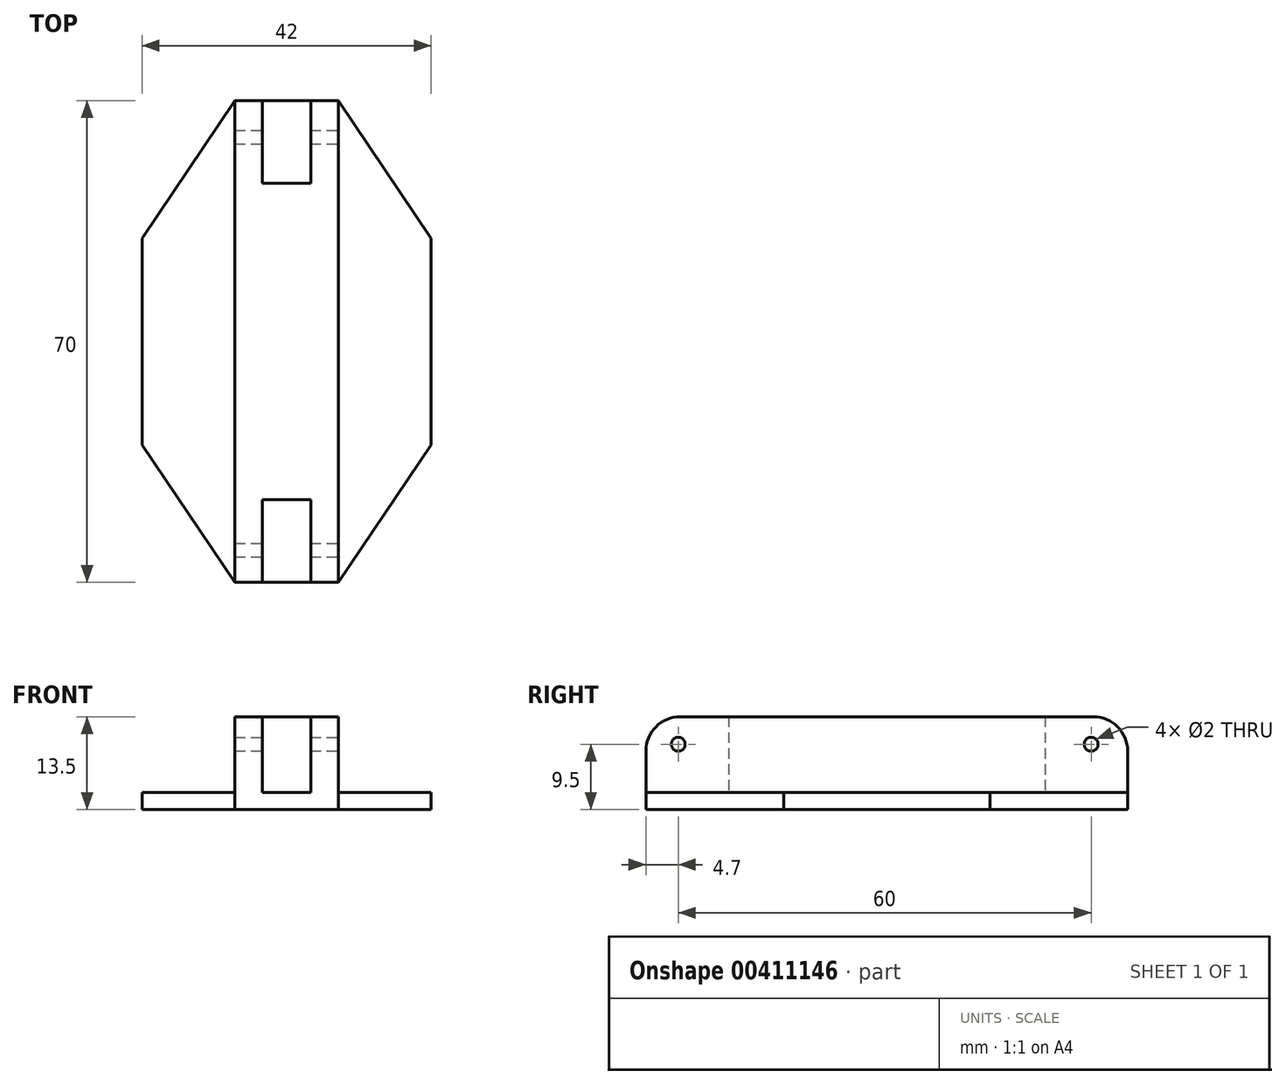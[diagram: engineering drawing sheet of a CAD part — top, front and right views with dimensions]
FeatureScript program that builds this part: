
annotation { "Feature Type Name" : "Feature", "Feature Type Description" : "" }
export const myFeature = defineFeature(function(context is Context, id is Id, definition is map)
    precondition{}
    {
        {
            var Q0;
            Q0=qCreatedBy(makeId("Top.planeOp"),FACE);
            var sketch = newSketch(context, id + "F0", { "sketchPlane" : qUnion([Q0])});
            skLineSegment(sketch, "E0.bottom", {"start": v(-7.14, 35.3) * mm, "end": v(7.86, 35.3) * mm});
            skLineSegment(sketch, "E0.top", {"start": v(-7.14, -34.7) * mm, "end": v(7.86, -34.7) * mm});
            skLineSegment(sketch, "E0.left", {"start": v(-20.64, 15.3) * mm, "end": v(-20.64, -14.7) * mm});
            skLineSegment(sketch, "E0.right", {"start": v(21.36, 15.3) * mm, "end": v(21.36, -14.7) * mm});
            skPoint(sketch, "E0.middle", {"position": v(0.36, 0.3) * mm});
            skLineSegment(sketch, "E1", {"start": v(-7.14, 35.3) * mm, "end": v(-7.14, 15.3) * mm});
            skLineSegment(sketch, "E2", {"start": v(-7.14, 15.3) * mm, "end": v(-20.64, 15.3) * mm});
            skLineSegment(sketch, "E3", {"start": v(7.86, 35.3) * mm, "end": v(7.86, 15.3) * mm});
            skLineSegment(sketch, "E4", {"start": v(7.86, 15.3) * mm, "end": v(21.36, 15.3) * mm});
            skLineSegment(sketch, "E5", {"start": v(-7.14, -34.7) * mm, "end": v(-7.14, -14.7) * mm});
            skLineSegment(sketch, "E6", {"start": v(-7.14, -14.7) * mm, "end": v(-20.64, -14.7) * mm});
            skLineSegment(sketch, "E7", {"start": v(7.86, -34.7) * mm, "end": v(7.86, -14.7) * mm});
            skLineSegment(sketch, "E8", {"start": v(7.86, -14.7) * mm, "end": v(21.36, -14.7) * mm});
            skPoint(sketch, "E9.orphan", {"position": v(-20.64, 35.3) * mm});
            skPoint(sketch, "E10.orphan", {"position": v(21.36, 35.3) * mm});
            skPoint(sketch, "E11.orphan", {"position": v(21.36, -34.7) * mm});
            skPoint(sketch, "E12.orphan", {"position": v(-20.64, -34.7) * mm});
            skLineSegment(sketch, "E13", {"start": v(-20.64, -14.7) * mm, "end": v(-7.14, -34.7) * mm});
            skLineSegment(sketch, "E14", {"start": v(-20.64, 15.3) * mm, "end": v(-7.14, 35.3) * mm});
            skLineSegment(sketch, "E15", {"start": v(7.86, 35.3) * mm, "end": v(21.36, 15.3) * mm});
            skLineSegment(sketch, "E16", {"start": v(21.36, -14.7) * mm, "end": v(7.86, -34.7) * mm});
            skLineSegment(sketch, "E17", {"start": v(-3.14, 35.3) * mm, "end": v(-3.14, 23.3) * mm});
            skLineSegment(sketch, "E18", {"start": v(3.86, 35.3) * mm, "end": v(3.86, 23.3) * mm});
            skLineSegment(sketch, "E19", {"start": v(3.86, 23.3) * mm, "end": v(-3.14, 23.3) * mm});
            skLineSegment(sketch, "E20", {"start": v(-3.14, -34.7) * mm, "end": v(-3.14, -22.7) * mm});
            skLineSegment(sketch, "E21", {"start": v(3.86, -34.7) * mm, "end": v(3.86, -22.7) * mm});
            skLineSegment(sketch, "E22", {"start": v(-3.14, -22.7) * mm, "end": v(3.86, -22.7) * mm});
            skLineSegment(sketch, "E23", {"start": v(-20.64, 12.3) * mm, "end": v(-7.14, 12.3) * mm});
            skLineSegment(sketch, "E24", {"start": v(-20.64, -11.7) * mm, "end": v(-7.14, -11.7) * mm});
            skLineSegment(sketch, "E25", {"start": v(21.36, 12.3) * mm, "end": v(7.86, 12.3) * mm});
            skLineSegment(sketch, "E26", {"start": v(21.36, -11.7) * mm, "end": v(7.86, -11.7) * mm});
            skLineSegment(sketch, "E27", {"start": v(-7.14, 12.3) * mm, "end": v(-7.14, -11.7) * mm});
            skLineSegment(sketch, "E28", {"start": v(7.86, 12.3) * mm, "end": v(7.86, -11.7) * mm});
            skLineSegment(sketch, "E29", {"start": v(7.86, 15.3) * mm, "end": v(7.86, 12.3) * mm});
            skLineSegment(sketch, "E30", {"start": v(-7.14, 15.3) * mm, "end": v(-7.14, 12.3) * mm});
            skLineSegment(sketch, "E31", {"start": v(7.86, -11.7) * mm, "end": v(7.86, -14.7) * mm});
            skLineSegment(sketch, "E32", {"start": v(-7.14, -11.7) * mm, "end": v(-7.14, -14.7) * mm});
            skLineSegment(sketch, "E33", {"start": v(16.36, 12.3) * mm, "end": v(16.36, -11.7) * mm});
            skLineSegment(sketch, "E34", {"start": v(-15.64, 12.3) * mm, "end": v(-15.64, -11.7) * mm});
            skPoint(sketch, "E34.endSnap0", {"position": v(-13.9, -11.7) * mm});
            skSolve(sketch);
        }
        {
            var Q0;
            {var subQ0=sQuery(id+"F0.wireOp",EDGE,"E28");Q0=makeQuery(id+"F0.imprint","IMPRINT",FACE,{"disambiguationData":[TD([[makeQuery(id+"F0.imprint","IMPRINT",EDGE,{"derivedFrom":subQ0}),1.0]])]});}
            var Q1;
            {var subQ1=sQuery(id+"F0.wireOp",EDGE,"E1");Q1=makeQuery(id+"F0.imprint","IMPRINT",FACE,{"disambiguationData":[TD([[makeQuery(id+"F0.imprint","IMPRINT",EDGE,{"derivedFrom":subQ1}),1.0]])]});}
            var Q2;
            {var subQ0=sQuery(id+"F0.wireOp",EDGE,"E17");Q2=makeQuery(id+"F0.imprint","IMPRINT",FACE,{"disambiguationData":[TD([[makeQuery(id+"F0.imprint","IMPRINT",EDGE,{"derivedFrom":subQ0}),1.0]])]});}
            var Q3;
            {var subQ0=sQuery(id+"F0.wireOp",EDGE,"E20");Q3=makeQuery(id+"F0.imprint","IMPRINT",FACE,{"disambiguationData":[TD([[makeQuery(id+"F0.imprint","IMPRINT",EDGE,{"derivedFrom":subQ0}),-1.0]])]});}
            var Q4;
            Q4=makeQuery(id+"F0.imprint","IMPRINT",FACE,{"disambiguationData":[TD([[makeQuery(id+"F0.imprint","IMPRINT",EDGE,{"derivedFrom":sQuery(id+"F0.wireOp",EDGE,"E1")}),-1.0]])]});
            var Q5;
            Q5=makeQuery(id+"F0.imprint","IMPRINT",FACE,{"disambiguationData":[TD([[makeQuery(id+"F0.imprint","IMPRINT",EDGE,{"derivedFrom":sQuery(id+"F0.wireOp",EDGE,"E3")}),1.0]])]});
            var Q6;
            Q6=makeQuery(id+"F0.imprint","IMPRINT",FACE,{"disambiguationData":[TD([[makeQuery(id+"F0.imprint","IMPRINT",EDGE,{"derivedFrom":sQuery(id+"F0.wireOp",EDGE,"E5")}),1.0]])]});
            var Q7;
            Q7=makeQuery(id+"F0.imprint","IMPRINT",FACE,{"disambiguationData":[TD([[makeQuery(id+"F0.imprint","IMPRINT",EDGE,{"derivedFrom":sQuery(id+"F0.wireOp",EDGE,"E7")}),-1.0]])]});
            var Q8;
            {var subQ5=sQuery(id+"F0.wireOp",EDGE,"E34");Q8=makeQuery(id+"F0.imprint","IMPRINT",FACE,{"disambiguationData":[TD([[makeQuery(id+"F0.imprint","IMPRINT",EDGE,{"derivedFrom":subQ5}),-1.0]])]});}
            var Q9;
            {var subQ5=sQuery(id+"F0.wireOp",EDGE,"E33");Q9=makeQuery(id+"F0.imprint","IMPRINT",FACE,{"disambiguationData":[TD([[makeQuery(id+"F0.imprint","IMPRINT",EDGE,{"derivedFrom":subQ5}),1.0]])]});}
            var Q10;
            {var subQ5=sQuery(id+"F0.wireOp",EDGE,"E2");Q10=makeQuery(id+"F0.imprint","IMPRINT",FACE,{"disambiguationData":[TD([[makeQuery(id+"F0.imprint","IMPRINT",EDGE,{"derivedFrom":subQ5}),1.0]])]});}
            var Q11;
            {var subQ5=sQuery(id+"F0.wireOp",EDGE,"E6");Q11=makeQuery(id+"F0.imprint","IMPRINT",FACE,{"disambiguationData":[TD([[makeQuery(id+"F0.imprint","IMPRINT",EDGE,{"derivedFrom":subQ5}),-1.0]])]});}
            var Q12;
            {var subQ3=sQuery(id+"F0.wireOp",EDGE,"E4");Q12=makeQuery(id+"F0.imprint","IMPRINT",FACE,{"disambiguationData":[TD([[makeQuery(id+"F0.imprint","IMPRINT",EDGE,{"derivedFrom":subQ3}),-1.0]])]});}
            var Q13;
            {var subQ3=sQuery(id+"F0.wireOp",EDGE,"E8");Q13=makeQuery(id+"F0.imprint","IMPRINT",FACE,{"disambiguationData":[TD([[makeQuery(id+"F0.imprint","IMPRINT",EDGE,{"derivedFrom":subQ3}),1.0]])]});}
            var Q14;
            {var subQ0=sQuery(id+"F0.wireOp",EDGE,"E27");Q14=makeQuery(id+"F0.imprint","IMPRINT",FACE,{"disambiguationData":[TD([[makeQuery(id+"F0.imprint","IMPRINT",EDGE,{"derivedFrom":subQ0}),-1.0]])]});}
            extrude(context, id + "F1", {"entities" : qUnion([Q0, Q1, Q2, Q3, Q4, Q5, Q6, Q7, Q8, Q9, Q10, Q11, Q12, Q13, Q14]), "depth" : 2.5 * mm});
        }
        {
            var Q0;
            {var subQ1=sQuery(id+"F0.wireOp",EDGE,"E1");Q0=makeQuery(id+"F0.imprint","IMPRINT",FACE,{"disambiguationData":[TD([[makeQuery(id+"F0.imprint","IMPRINT",EDGE,{"derivedFrom":subQ1}),1.0]])]});}
            extrude(context, id + "F2", {"entities" : qUnion([Q0]), "operationType" : NewBodyOperationType.ADD, "depth" : 13.5 * mm});
        }
        {
            var Q0;
            Q0=qCreatedBy(makeId("Right.planeOp"),FACE);
            var sketch = newSketch(context, id + "F3", { "sketchPlane" : qUnion([Q0])});
            skCircle(sketch, "E35", {"center": v(-30, 9.5) * mm, "radius": 1 * mm});
            skCircle(sketch, "E36.MirrorC", {"center": v(30, 9.5) * mm, "radius": 1 * mm});
            skSolve(sketch);
        }
        {
            var Q0;
            Q0 = qSketchRegion(id + "F3", true);
            extrude(context, id + "F4", {"entities" : qUnion([Q0]), "operationType" : NewBodyOperationType.REMOVE, "endBound" : BoundingType.SYMMETRIC, "oppositeDirection" : true, "depth" : 25 * mm});
        }
        {
            var Q0;
            {var subQ0=sQuery(id+"F0.wireOp",EDGE,"E0.top");Q0=makeQuery(id+"F2.opExtrude","CAP_EDGE",EDGE,{"disambiguationData":[OSD([subQ0]),TDD([makeQuery(id+"F0.imprint","IMPRINT",EDGE,{"disambiguationData":[TD([[makeQuery(id+"F0.imprint","INTERSECT",VERTEX,{"derivedFrom":[subQ0,sQuery(id+"F0.wireOp",EDGE,"E20")]}),1.0]])],"derivedFrom":subQ0})])],"isStart":false});}
            var Q1;
            {var subQ0=sQuery(id+"F0.wireOp",EDGE,"E0.top");Q1=makeQuery(id+"F2.opExtrude","CAP_EDGE",EDGE,{"disambiguationData":[OSD([subQ0]),TDD([makeQuery(id+"F0.imprint","IMPRINT",EDGE,{"disambiguationData":[TD([[makeQuery(id+"F0.imprint","INTERSECT",VERTEX,{"derivedFrom":[subQ0,sQuery(id+"F0.wireOp",EDGE,"E21")]}),-1.0]])],"derivedFrom":subQ0})])],"isStart":false});}
            fillet(context, id + "F5", {"entities" : qUnion([Q0, Q1]), "radius" : 5 * mm, "tangentPropagation" : true, "allowEdgeOverflow" : false});
        }
        {
            var Q0;
            {var subQ0=sQuery(id+"F0.wireOp",EDGE,"E0.bottom");Q0=makeQuery(id+"F2.opExtrude","CAP_EDGE",EDGE,{"disambiguationData":[OSD([subQ0]),TDD([makeQuery(id+"F0.imprint","IMPRINT",EDGE,{"disambiguationData":[TD([[makeQuery(id+"F0.imprint","INTERSECT",VERTEX,{"derivedFrom":[subQ0,sQuery(id+"F0.wireOp",EDGE,"E18")]}),-1.0]])],"derivedFrom":subQ0})])],"isStart":false});}
            var Q1;
            {var subQ0=sQuery(id+"F0.wireOp",EDGE,"E0.bottom");Q1=makeQuery(id+"F2.opExtrude","CAP_EDGE",EDGE,{"disambiguationData":[OSD([subQ0]),TDD([makeQuery(id+"F0.imprint","IMPRINT",EDGE,{"disambiguationData":[TD([[makeQuery(id+"F0.imprint","INTERSECT",VERTEX,{"derivedFrom":[subQ0,sQuery(id+"F0.wireOp",EDGE,"E17")]}),1.0]])],"derivedFrom":subQ0})])],"isStart":false});}
            fillet(context, id + "F6", {"entities" : qUnion([Q0, Q1]), "radius" : 5 * mm, "tangentPropagation" : true, "allowEdgeOverflow" : false});
        }
    });
